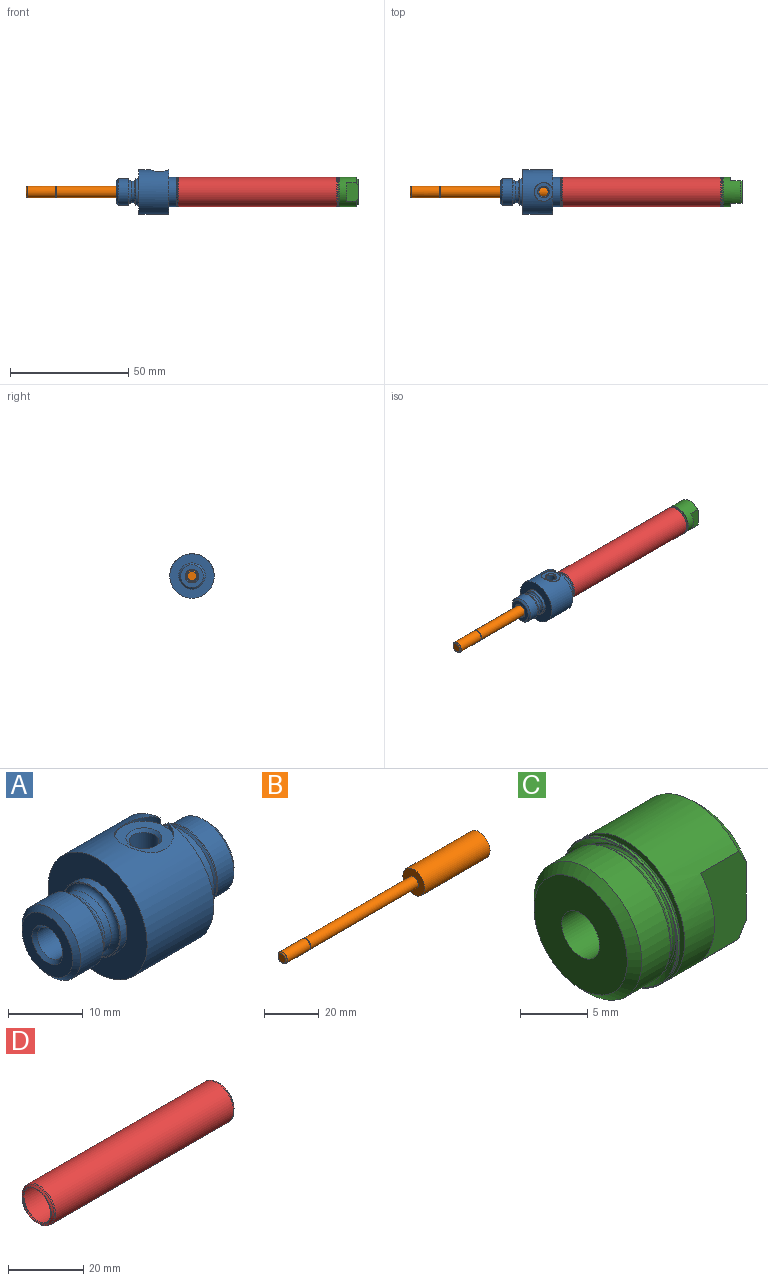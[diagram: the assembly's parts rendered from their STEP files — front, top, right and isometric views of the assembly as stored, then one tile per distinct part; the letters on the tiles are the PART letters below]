
ASSEMBLY  parts=4 mates=3
PART A: 31 faces, bbox 30.2x18.7x18.7 mm
  f0: cylinder r=1.98mm len=5.52mm, axis (0,0,-1), area 68.8mm2, adj f1,f30
  f1: cone r=1.98mm half-angle=45deg, axis (0,0,1), area 8.4mm2, adj f0,f2
  f2: plane 7.92x7.84mm, normal (0,0,1), area 30.9mm2, adj f1,f3,f4
  f3: cylinder r=3.96mm len=7.92mm, axis (0,0,-1), area 12.8mm2, adj f2,f4,f13
  f4: plane 18.75x18.71mm, normal (1,0,0), area 154.9mm2, adj f2,f3,f5,f13
  f5: cylinder r=6.17mm len=12.33mm, axis (-1,0,0), area 125.5mm2, adj f4,f12
  f6: cone r=6.17mm half-angle=45deg, axis (1,0,0), area 26.6mm2, adj f11,f12
  f7: cone r=5.16mm half-angle=45deg, axis (-1,0,0), area 6.6mm2, adj f8,f29
  f8: torus R=5.39mm, axis (1,0,0), area 6.8mm2, adj f7,f9
  f9: cone r=5.48mm half-angle=45deg, axis (1,0,0), area 30.7mm2, adj f8,f10
  f10: plane 12.33x12.33mm, normal (1,0,0), area 3.2mm2, adj f9,f11
  f11: cylinder r=6.17mm len=12.33mm, axis (-1,0,0), area 7.9mm2, adj f6,f10
  f12: plane 12.33x12.33mm, normal (1,0,0), area 18.8mm2, adj f5,f6
  f13: cylinder r=9.37mm len=18.75mm, axis (-1,0,0), area 695.1mm2, adj f3,f4,f14
  f14: plane 18.75x18.75mm, normal (-1,0,0), area 180.1mm2, adj f13,f15
  f15: cylinder r=5.52mm len=11.05mm, axis (-1,0,0), area 41.9mm2, adj f14,f16
  f16: plane 11.05x11.05mm, normal (-1,0,0), area 5.2mm2, adj f15,f17
  f17: torus R=5.37mm, axis (1,0,0), area 38.4mm2, adj f16,f18
  f18: cylinder r=4.57mm len=9.14mm, axis (-1,0,0), area 33.6mm2, adj f17,f19
  f19: torus R=5.37mm, axis (1,0,0), area 18.3mm2, adj f18,f20
  f20: cone r=5.56mm half-angle=44.8deg, axis (-1,0,0), area 34.7mm2, adj f19,f21
  f21: cylinder r=5.56mm len=11.11mm, axis (-1,0,0), area 149.2mm2, adj f20,f22
  f22: cone r=4.8mm half-angle=45deg, axis (1,0,0), area 34.8mm2, adj f21,f23
  f23: plane 9.6x9.6mm, normal (-1,0,0), area 45.7mm2, adj f22,f24
  f24: cone r=2.91mm half-angle=45deg, axis (-1,0,0), area 12mm2, adj f23,f30
  f25: plane 10.33x10.33mm, normal (1,0,0), area 65.5mm2, adj f26,f30
  f26: cone r=5.67mm half-angle=45deg, axis (-1,0,0), area 24.5mm2, adj f25,f27
  f27: cylinder r=5.67mm len=11.34mm, axis (-1,0,0), area 115.8mm2, adj f26,f28
  f28: cone r=5.16mm half-angle=45deg, axis (1,0,0), area 24.5mm2, adj f27,f29
  f29: cylinder r=5.16mm len=10.33mm, axis (-1,0,0), area 8.2mm2, adj f7,f28
  f30: cylinder r=2.41mm len=29.67mm, axis (-1,0,0), area 434.8mm2, adj f0,f24,f25
PART B: 10 faces, bbox 102.1x11.2x11.2 mm
  f0: cylinder r=2.16mm len=4.32mm, axis (-1,0,0), area 3.4mm2, adj f1,f2
  f1: plane 4.83x4.83mm, normal (1,0,0), area 3.6mm2, adj f0,f9
  f2: plane 4.75x4.75mm, normal (-1,0,0), area 3.1mm2, adj f0,f4
  f3: plane 11.24x11.24mm, normal (1,0,0), area 99.2mm2, adj f6
  f4: cylinder r=2.37mm len=55.58mm, axis (-1,0,0), area 829.3mm2, adj f2,f5
  f5: plane 11.24x11.24mm, normal (-1,0,0), area 81.5mm2, adj f4,f6
  f6: cylinder r=5.62mm len=33.83mm, axis (-1,0,0), area 1194.6mm2, adj f3,f5
  f7: plane 3.88x3.88mm, normal (-1,0,0), area 11.8mm2, adj f8
  f8: cone r=1.94mm half-angle=45deg, axis (1,0,0), area 9.1mm2, adj f7,f9
  f9: cylinder r=2.41mm len=11.97mm, axis (-1,0,0), area 181.5mm2, adj f1,f8
PART C: 24 faces, bbox 12.8x12.4x12.4 mm
  f0: plane 8.1x4.89mm, normal (0,1,0), area 37.2mm2, adj f4,f5,f12,f18,f19
  f1: plane 8.1x4.89mm, normal (0,-1,0), area 37.2mm2, adj f4,f5,f13,f18,f19
  f2: cylinder r=6.17mm len=12.33mm, axis (-1,0,0), area 7.9mm2, adj f3,f23
  f3: plane 12.33x12.33mm, normal (-1,0,0), area 3.2mm2, adj f2,f22
  f4: cylinder r=6.17mm len=12.33mm, axis (-1,0,0), area 207.8mm2, adj f0,f1,f5,f6,f12,f13,f19
  f5: cone r=6.17mm half-angle=45deg, axis (-1,0,0), area 11.9mm2, adj f0,f1,f4,f18
  f6: plane 12.33x12.33mm, normal (-1,0,0), area 18.8mm2, adj f4,f23
  f7: cylinder r=5.16mm len=10.33mm, axis (-1,0,0), area 8.2mm2, adj f8,f20
  f8: cone r=5.67mm half-angle=45deg, axis (-1,0,0), area 24.5mm2, adj f7,f9
  f9: cylinder r=5.67mm len=11.34mm, axis (-1,0,0), area 106.8mm2, adj f8,f10
  f10: cone r=4.91mm half-angle=45deg, axis (1,0,0), area 35.8mm2, adj f9,f11
  f11: plane 9.82x9.82mm, normal (-1,0,0), area 63.3mm2, adj f10,f15
  f12: plane 7.98x1.47mm, normal (1,0,0), area 8mm2, adj f0,f4
  f13: plane 7.98x1.47mm, normal (1,0,0), area 8mm2, adj f1,f4
  f14: cone r=1.98mm half-angle=45deg, axis (1,0,0), area 8.4mm2, adj f15,f17
  f15: cylinder r=1.98mm len=11.89mm, axis (-1,0,0), area 148.2mm2, adj f11,f14
  f16: cylinder r=3.96mm len=7.92mm, axis (-1,0,0), area 9.5mm2, adj f17,f18
  f17: plane 7.92x7.92mm, normal (1,0,0), area 31mm2, adj f14,f16
  f18: plane 10.81x9.4mm, normal (1,0,0), area 37.3mm2, adj f0,f1,f5,f16,f19
  f19: cone r=6.17mm half-angle=45deg, axis (-1,0,0), area 11.9mm2, adj f0,f1,f4,f18
  f20: cone r=5.3mm half-angle=45deg, axis (1,0,0), area 6.6mm2, adj f7,f21
  f21: torus R=5.39mm, axis (1,0,0), area 6.8mm2, adj f20,f22
  f22: cone r=6.08mm half-angle=45deg, axis (-1,0,0), area 30.7mm2, adj f3,f21
  f23: cone r=5.66mm half-angle=45deg, axis (-1,0,0), area 26.6mm2, adj f2,f6
PART D: 14 faces, bbox 68.6x13.3x13.3 mm
  f0: cone r=6.02mm half-angle=45deg, axis (1,0,0), area 27.2mm2, adj f1,f13
  f1: torus R=5.39mm, axis (1,0,0), area 6.8mm2, adj f0,f2
  f2: cone r=5.3mm half-angle=45deg, axis (-1,0,0), area 6.6mm2, adj f1,f3
  f3: cylinder r=5.16mm len=10.33mm, axis (-1,0,0), area 8.2mm2, adj f2,f4
  f4: cone r=5.16mm half-angle=45deg, axis (1,0,0), area 24.5mm2, adj f3,f5
  f5: cylinder r=5.67mm len=66.75mm, axis (-1,0,0), area 2378.3mm2, adj f4,f6
  f6: cone r=5.67mm half-angle=45deg, axis (-1,0,0), area 24.5mm2, adj f5,f7
  f7: cylinder r=5.16mm len=10.33mm, axis (-1,0,0), area 8.2mm2, adj f6,f8
  f8: cone r=5.16mm half-angle=45deg, axis (1,0,0), area 6.6mm2, adj f7,f9
  f9: torus R=5.39mm, axis (1,0,0), area 6.8mm2, adj f8,f10
  f10: cone r=5.48mm half-angle=45deg, axis (-1,0,0), area 27.2mm2, adj f9,f11
  f11: torus R=5.66mm, axis (1,0,0), area 15.3mm2, adj f10,f12
  f12: cylinder r=6.17mm len=66.78mm, axis (-1,0,0), area 2587mm2, adj f11,f13
  f13: torus R=5.66mm, axis (1,0,0), area 15.3mm2, adj f0,f12
PLACE A at identity fixed
PLACE B t=(-25.41,0,0)mm
PLACE C t=(89.41,0,0)mm
PLACE D t=(25.91,0,0)mm
MATE fastened C.f4 <-> A.f5  axis (-1,0,0) through (89.41,0,0)mm
MATE fastened D.f0 <-> A.f5  axis (-1,0,0) through (59.79,0,0)mm
MATE slider B.f0 <-> A.f5  axis (-1,0,0) through (2.38,0,0)mm
